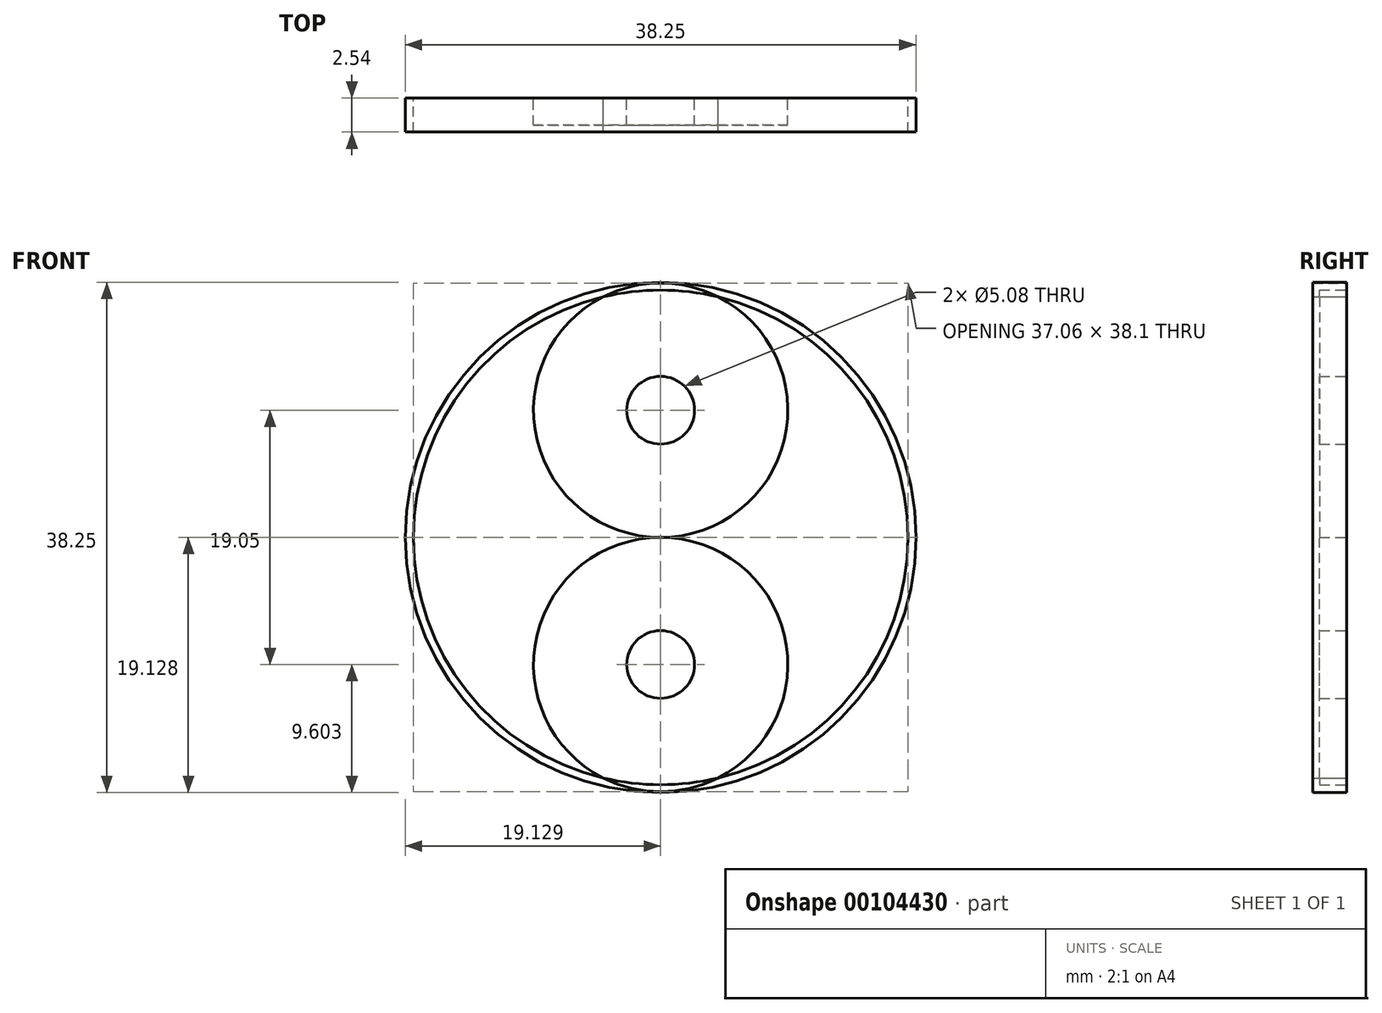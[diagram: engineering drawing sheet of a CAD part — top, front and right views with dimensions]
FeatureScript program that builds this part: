
annotation { "Feature Type Name" : "Feature", "Feature Type Description" : "" }
export const myFeature = defineFeature(function(context is Context, id is Id, definition is map)
    precondition{}
    {
        {
            var Q0;
            Q0=qCreatedBy(makeId("Front.planeOp"),FACE);
            var sketch = newSketch(context, id + "F0", { "sketchPlane" : qUnion([Q0])});
            skCircle(sketch, "E0", {"center": v(21.8, 8.56) * mm, "radius": 19.13 * mm});
            skCircle(sketch, "E1", {"center": v(21.8, 8.56) * mm, "radius": 18.53 * mm});
            skLineSegment(sketch, "E2", {"start": v(21.8, 8.56) * mm, "end": v(21.8, 8.56) * mm});
            skCircle(sketch, "E3", {"center": v(21.8, 18.08) * mm, "radius": 2.54 * mm});
            skCircle(sketch, "E4", {"center": v(21.8, -0.97) * mm, "radius": 2.54 * mm});
            skCircle(sketch, "E5", {"center": v(21.8, 18.08) * mm, "radius": 9.53 * mm});
            skCircle(sketch, "E6", {"center": v(21.8, -0.97) * mm, "radius": 9.53 * mm});
            skSolve(sketch);
        }
        {
            var Q0;
            {var subQ0=sQuery(id+"F0.wireOp",EDGE,"E5");var subQ1=sQuery(id+"F0.wireOp",EDGE,"E1");var subQ2=makeQuery(id+"F0.imprint","INTERSECT",VERTEX,{"disambiguationData":[OD(0.0)],"derivedFrom":[subQ1,subQ0]});Q0=makeQuery(id+"F0.imprint","IMPRINT",FACE,{"disambiguationData":[TD([[makeQuery(id+"F0.imprint","IMPRINT",EDGE,{"disambiguationData":[TD([[subQ2,-1.0]])],"derivedFrom":subQ1}),1.0]])]});}
            var Q1;
            Q1=makeQuery(id+"F0.imprint","IMPRINT",FACE,{"disambiguationData":[TD([[makeQuery(id+"F0.imprint","IMPRINT",EDGE,{"derivedFrom":sQuery(id+"F0.wireOp",EDGE,"E3")}),-1.0]])]});
            var Q2;
            Q2=makeQuery(id+"F0.imprint","IMPRINT",FACE,{"disambiguationData":[TD([[makeQuery(id+"F0.imprint","IMPRINT",EDGE,{"derivedFrom":sQuery(id+"F0.wireOp",EDGE,"E4")}),1.0]])]});
            extrude(context, id + "F1", {"entities" : qUnion([Q0, Q1, Q2]), "depth" : 2.03 * mm});
        }
        {
            var Q0;
            {var subQ0=sQuery(id+"F0.wireOp",EDGE,"E5");var subQ1=sQuery(id+"F0.wireOp",EDGE,"E1");var subQ2=makeQuery(id+"F0.imprint","INTERSECT",VERTEX,{"disambiguationData":[OD(1.0)],"derivedFrom":[subQ1,subQ0]});Q0=makeQuery(id+"F0.imprint","IMPRINT",FACE,{"disambiguationData":[TD([[makeQuery(id+"F0.imprint","IMPRINT",EDGE,{"disambiguationData":[TD([[subQ2,1.0]])],"derivedFrom":subQ1}),1.0]])]});}
            var Q1;
            Q1=makeQuery(id+"F0.imprint","IMPRINT",FACE,{"disambiguationData":[TD([[makeQuery(id+"F0.imprint","IMPRINT",EDGE,{"derivedFrom":sQuery(id+"F0.wireOp",EDGE,"E4")}),-1.0]])]});
            var Q2;
            Q2=makeQuery(id+"F0.imprint","IMPRINT",FACE,{"disambiguationData":[TD([[makeQuery(id+"F0.imprint","IMPRINT",EDGE,{"derivedFrom":sQuery(id+"F0.wireOp",EDGE,"E3")}),1.0]])]});
            extrude(context, id + "F2", {"entities" : qUnion([Q0, Q1, Q2]), "depth" : 2.03 * mm});
        }
        {
            var Q0;
            Q0=makeQuery(id+"F0.imprint","IMPRINT",FACE,{"disambiguationData":[TD([[makeQuery(id+"F0.imprint","IMPRINT",EDGE,{"derivedFrom":sQuery(id+"F0.wireOp",EDGE,"E0")}),1.0]])]});
            extrude(context, id + "F3", {"entities" : qUnion([Q0]), "depth" : 2.54 * mm});
        }
    });
